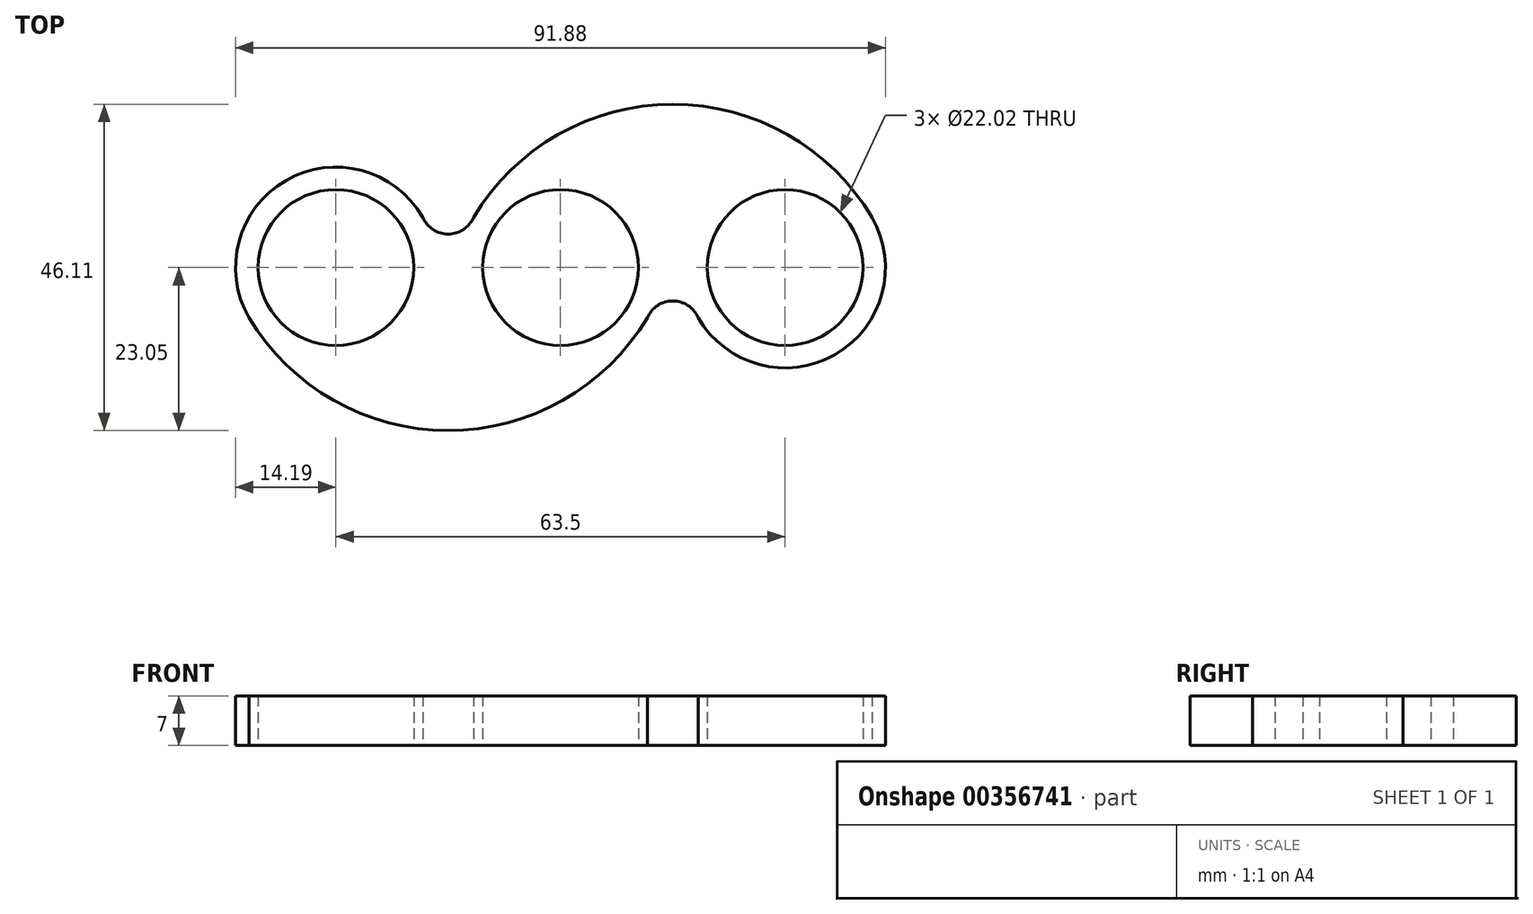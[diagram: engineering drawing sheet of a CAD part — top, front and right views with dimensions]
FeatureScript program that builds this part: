
annotation { "Feature Type Name" : "Feature", "Feature Type Description" : "" }
export const myFeature = defineFeature(function(context is Context, id is Id, definition is map)
    precondition{}
    {
        {
            var Q0;
            Q0=qCreatedBy(makeId("Top.planeOp"),FACE);
            var sketch = newSketch(context, id + "F0", { "sketchPlane" : qUnion([Q0])});
            skCircle(sketch, "E0", {"center": v(0, 0) * mm, "radius": 11.01 * mm});
            skCircle(sketch, "E1", {"center": v(0, 0) * mm, "radius": 14.19 * mm});
            skCircle(sketch, "E2", {"center": v(-31.75, 0) * mm, "radius": 11.01 * mm});
            skCircle(sketch, "E3", {"center": v(-31.75, 0) * mm, "radius": 14.19 * mm});
            skCircle(sketch, "E4", {"center": v(31.75, 0) * mm, "radius": 11.01 * mm});
            skCircle(sketch, "E5", {"center": v(31.75, 0) * mm, "radius": 14.19 * mm});
            skLineSegment(sketch, "E6", {"start": v(0, 0) * mm, "end": v(31.75, 0) * mm});
            skLineSegment(sketch, "E7", {"start": v(0, 0) * mm, "end": v(-31.75, 0) * mm});
            skPoint(sketch, "E8", {"position": v(-19.46, 7.1) * mm});
            skPoint(sketch, "E9", {"position": v(-12.29, 7.1) * mm});
            skPoint(sketch, "E10", {"position": v(-44.04, -7.1) * mm});
            skPoint(sketch, "E11", {"position": v(12.29, -7.1) * mm});
            skPoint(sketch, "E12", {"position": v(19.46, -7.1) * mm});
            skPoint(sketch, "E13", {"position": v(44.04, 7.1) * mm});
            skPoint(sketch, "E14", {"position": v(-15.88, 4.72) * mm});
            skArc(sketch, "E15", {"start": v(-19.46, 7.1) * mm, "mid": v(-15.88, 4.72) * mm, "end": v(-12.29, 7.1) * mm});
            skPoint(sketch, "E16", {"position": v(-15.88, -23.05) * mm});
            skArc(sketch, "E17", {"start": v(-44.04, -7.1) * mm, "mid": v(-15.88, -23.05) * mm, "end": v(12.29, -7.1) * mm});
            skPoint(sketch, "E18", {"position": v(15.88, -4.72) * mm});
            skPoint(sketch, "E19", {"position": v(15.87, 23.06) * mm});
            skArc(sketch, "E20", {"start": v(44.04, 7.1) * mm, "mid": v(15.87, 23.06) * mm, "end": v(-12.29, 7.1) * mm});
            skArc(sketch, "E21", {"start": v(19.46, -7.1) * mm, "mid": v(15.88, -4.72) * mm, "end": v(12.29, -7.1) * mm});
            skSolve(sketch);
        }
        {
            var Q0;
            Q0=makeQuery(id+"F0.imprint","IMPRINT",FACE,{"disambiguationData":[TD([[makeQuery(id+"F0.imprint","IMPRINT",EDGE,{"derivedFrom":sQuery(id+"F0.wireOp",EDGE,"E2")}),-1.0]])]});
            var Q1;
            {var subQ0=sQuery(id+"F0.wireOp",EDGE,"E17");var subQ1=sQuery(id+"F0.wireOp",EDGE,"E1");var subQ2=makeQuery(id+"F0.imprint","INTERSECT",VERTEX,{"derivedFrom":[subQ1,subQ0]});Q1=makeQuery(id+"F0.imprint","IMPRINT",FACE,{"disambiguationData":[TD([[makeQuery(id+"F0.imprint","IMPRINT",EDGE,{"disambiguationData":[TD([[subQ2,1.0]])],"derivedFrom":subQ1}),-1.0]])]});}
            var Q2;
            {var subQ0=sQuery(id+"F0.wireOp",EDGE,"E15");var subQ1=sQuery(id+"F0.wireOp",EDGE,"E1");var subQ2=makeQuery(id+"F0.imprint","INTERSECT",VERTEX,{"derivedFrom":[subQ1,subQ0]});Q2=makeQuery(id+"F0.imprint","IMPRINT",FACE,{"disambiguationData":[TD([[makeQuery(id+"F0.imprint","IMPRINT",EDGE,{"disambiguationData":[TD([[subQ2,-1.0]])],"derivedFrom":subQ1}),-1.0]])]});}
            var Q3;
            {var subQ0=sQuery(id+"F0.wireOp",EDGE,"E6");var subQ1=sQuery(id+"F0.wireOp",EDGE,"E0");var subQ2=makeQuery(id+"F0.imprint","INTERSECT",VERTEX,{"derivedFrom":[subQ1,subQ0]});Q3=makeQuery(id+"F0.imprint","IMPRINT",FACE,{"disambiguationData":[TD([[makeQuery(id+"F0.imprint","IMPRINT",EDGE,{"disambiguationData":[TD([[subQ2,1.0]])],"derivedFrom":subQ1}),-1.0]])]});}
            var Q4;
            {var subQ0=sQuery(id+"F0.wireOp",EDGE,"E6");var subQ1=sQuery(id+"F0.wireOp",EDGE,"E0");var subQ2=makeQuery(id+"F0.imprint","INTERSECT",VERTEX,{"derivedFrom":[subQ1,subQ0]});Q4=makeQuery(id+"F0.imprint","IMPRINT",FACE,{"disambiguationData":[TD([[makeQuery(id+"F0.imprint","IMPRINT",EDGE,{"disambiguationData":[TD([[subQ2,-1.0]])],"derivedFrom":subQ1}),-1.0]])]});}
            var Q5;
            {var subQ0=sQuery(id+"F0.wireOp",EDGE,"E20");var subQ1=sQuery(id+"F0.wireOp",EDGE,"E1");var subQ2=makeQuery(id+"F0.imprint","INTERSECT",VERTEX,{"derivedFrom":[subQ1,subQ0]});Q5=makeQuery(id+"F0.imprint","IMPRINT",FACE,{"disambiguationData":[TD([[makeQuery(id+"F0.imprint","IMPRINT",EDGE,{"disambiguationData":[TD([[subQ2,1.0]])],"derivedFrom":subQ1}),-1.0]])]});}
            var Q6;
            {var subQ0=sQuery(id+"F0.wireOp",EDGE,"E21");var subQ1=sQuery(id+"F0.wireOp",EDGE,"E1");var subQ2=makeQuery(id+"F0.imprint","INTERSECT",VERTEX,{"derivedFrom":[subQ1,subQ0]});Q6=makeQuery(id+"F0.imprint","IMPRINT",FACE,{"disambiguationData":[TD([[makeQuery(id+"F0.imprint","IMPRINT",EDGE,{"disambiguationData":[TD([[subQ2,-1.0]])],"derivedFrom":subQ1}),-1.0]])]});}
            var Q7;
            Q7=makeQuery(id+"F0.imprint","IMPRINT",FACE,{"disambiguationData":[TD([[makeQuery(id+"F0.imprint","IMPRINT",EDGE,{"derivedFrom":sQuery(id+"F0.wireOp",EDGE,"E4")}),-1.0]])]});
            extrude(context, id + "F1", {"entities" : qUnion([Q0, Q1, Q2, Q3, Q4, Q5, Q6, Q7]), "depth" : 7 * mm});
        }
    });
